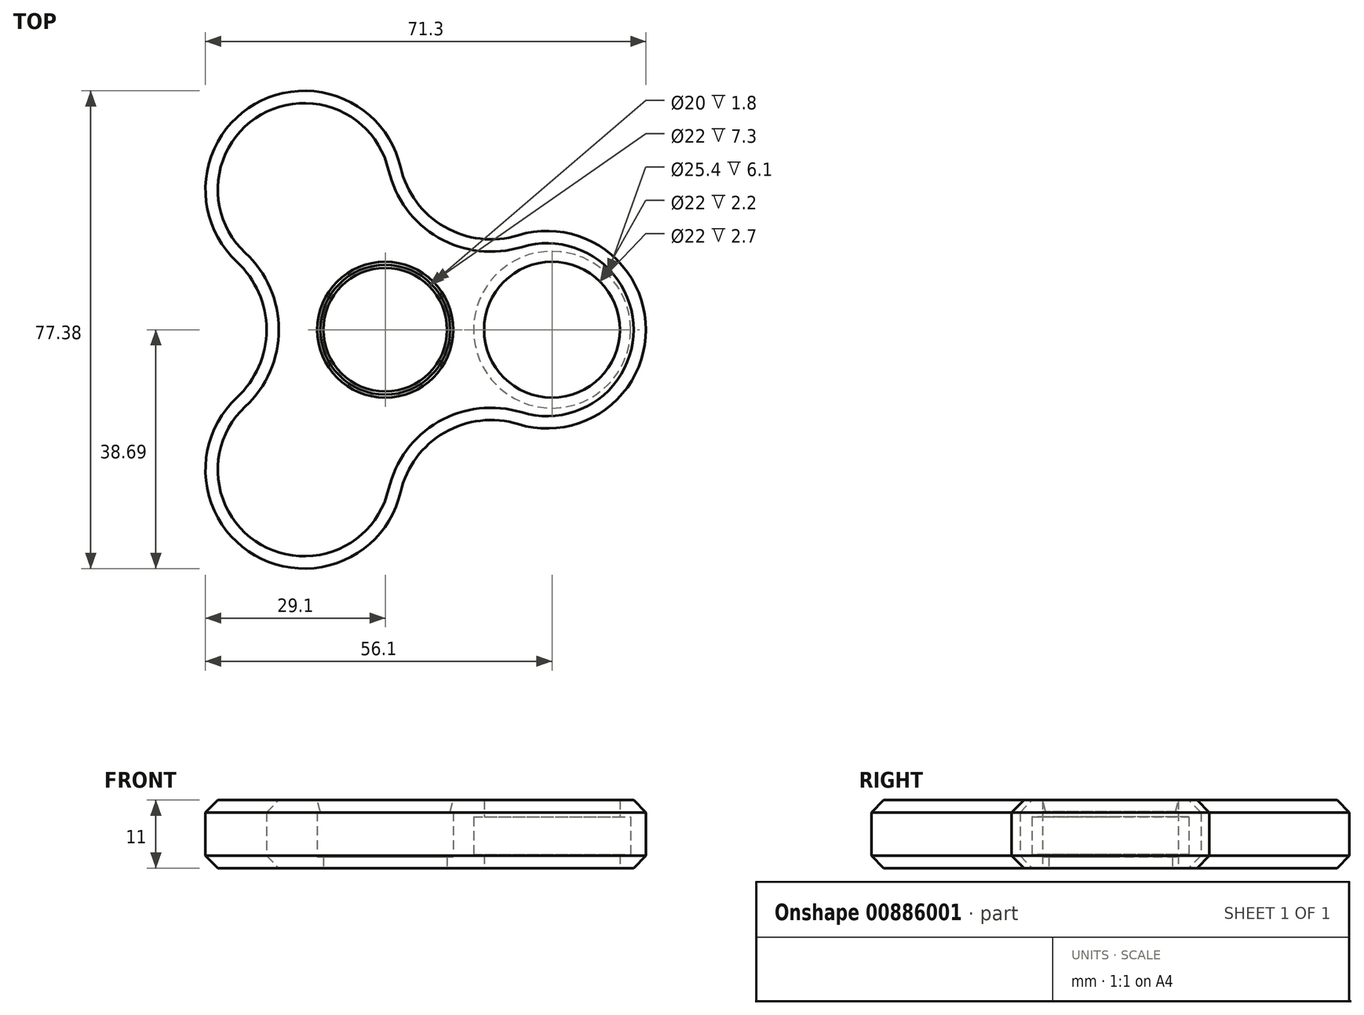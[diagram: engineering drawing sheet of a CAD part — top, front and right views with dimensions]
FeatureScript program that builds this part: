
annotation { "Feature Type Name" : "Feature", "Feature Type Description" : "" }
export const myFeature = defineFeature(function(context is Context, id is Id, definition is map)
    precondition{}
    {
        {
            var Q0;
            Q0=qCreatedBy(makeId("Top.planeOp"),FACE);
            var sketch = newSketch(context, id + "F0", { "sketchPlane" : qUnion([Q0])});
            skLineSegment(sketch, "E0", {"start": v(0, 0) * mm, "end": v(26.2, 0) * mm, "construction": true});
            skCircle(sketch, "E1", {"center": v(0, 0) * mm, "radius": 26.2 * mm, "construction": true});
            skLineSegment(sketch, "E2", {"start": v(0, 0) * mm, "end": v(-13.1, 22.69) * mm, "construction": true});
            skLineSegment(sketch, "E3", {"start": v(0, 0) * mm, "end": v(-13.1, -22.69) * mm, "construction": true});
            skArc(sketch, "E4", {"start": v(21.5, -15.3) * mm, "mid": v(42.2, 0) * mm, "end": v(21.5, 15.3) * mm});
            skArc(sketch, "E5", {"start": v(2.5, 26.28) * mm, "mid": v(-21.1, 36.55) * mm, "end": v(-24, 10.98) * mm});
            skArc(sketch, "E6", {"start": v(-24, -10.98) * mm, "mid": v(-21.1, -36.55) * mm, "end": v(2.5, -26.28) * mm});
            skArc(sketch, "E7", {"start": v(2.5, 26.28) * mm, "mid": v(9.61, 16.65) * mm, "end": v(21.5, 15.3) * mm});
            skArc(sketch, "E8.1.0", {"start": v(-24, -10.98) * mm, "mid": v(-19.22, 0) * mm, "end": v(-24, 10.98) * mm});
            skArc(sketch, "E8.2.0", {"start": v(21.5, -15.3) * mm, "mid": v(9.61, -16.65) * mm, "end": v(2.5, -26.28) * mm});
            skSolve(sketch);
        }
        {
            var Q0;
            Q0=qSketchRegion(id+"F0",true);
            extrude(context, id + "F1", {"entities" : qUnion([Q0]), "depth" : 11 * mm, "offsetDistance" : 25 * mm});
        }
        {
            var Q0;
            Q0=qCreatedBy(makeId("Right.planeOp"),FACE);
            var sketch = newSketch(context, id + "F2", { "sketchPlane" : qUnion([Q0])});
            skLineSegment(sketch, "E9", {"start": v(0, 0) * mm, "end": v(0, 11) * mm});
            skLineSegment(sketch, "E10", {"start": v(0, 11) * mm, "end": v(11, 11) * mm});
            skLineSegment(sketch, "E11", {"start": v(11, 11) * mm, "end": v(10.5, 9.1) * mm});
            skLineSegment(sketch, "E12", {"start": v(10.5, 9.1) * mm, "end": v(11, 9.1) * mm});
            skLineSegment(sketch, "E13", {"start": v(11, 9.1) * mm, "end": v(11, 1.8) * mm});
            skLineSegment(sketch, "E14", {"start": v(11, 1.8) * mm, "end": v(10, 1.8) * mm});
            skLineSegment(sketch, "E15", {"start": v(10, 1.8) * mm, "end": v(10, 0) * mm});
            skLineSegment(sketch, "E16", {"start": v(10, 0) * mm, "end": v(0, 0) * mm});
            skLineSegment(sketch, "E17", {"start": v(0, 17.58) * mm, "end": v(0, -10.03) * mm, "construction": true});
            skSolve(sketch);
        }
        {
            var Q0;
            Q0=qSketchRegion(id+"F2",true);
            var Q1;
            Q1=sQuery(id+"F2.wireOp",EDGE,"E17");
            revolve(context, id + "F3", {"operationType" : NewBodyOperationType.REMOVE, "surfaceOperationType" : NewSurfaceOperationType.NEW, "entities" : qUnion([Q0]), "axis" : qUnion([Q1]), "revolveType" : RevolveType.FULL, "oppositeDirection" : true});
        }
        {
            var Q0;
            Q0=qCreatedBy(makeId("Front.planeOp"),FACE);
            var sketch = newSketch(context, id + "F4", { "sketchPlane" : qUnion([Q0])});
            skLineSegment(sketch, "E18", {"start": v(27, 31.94) * mm, "end": v(27, -19.35) * mm, "construction": true});
            skLineSegment(sketch, "E19", {"start": v(27, 0) * mm, "end": v(27, 11) * mm});
            skLineSegment(sketch, "E20", {"start": v(27, 11) * mm, "end": v(14.3, 11) * mm});
            skLineSegment(sketch, "E21", {"start": v(16, 8.3) * mm, "end": v(14.3, 8.3) * mm});
            skLineSegment(sketch, "E22", {"start": v(14.3, 8.3) * mm, "end": v(14.3, 2.2) * mm});
            skLineSegment(sketch, "E23", {"start": v(14.3, 2.2) * mm, "end": v(16, 2.2) * mm});
            skLineSegment(sketch, "E24", {"start": v(16, 2.2) * mm, "end": v(16, 0) * mm});
            skLineSegment(sketch, "E25", {"start": v(16, 0) * mm, "end": v(27, 0) * mm});
            skLineSegment(sketch, "E26", {"start": v(16, 8.3) * mm, "end": v(16, 11) * mm});
            skSolve(sketch);
        }
        {
            var Q0;
            Q0=qSketchRegion(id+"F4",true);
            var Q1;
            Q1=sQuery(id+"F4.wireOp",EDGE,"E18");
            revolve(context, id + "F5", {"operationType" : NewBodyOperationType.REMOVE, "surfaceOperationType" : NewSurfaceOperationType.NEW, "entities" : qUnion([Q0]), "axis" : qUnion([Q1]), "revolveType" : RevolveType.FULL, "oppositeDirection" : true});
        }
        {
            var Q0;
            Q0=makeQuery(id+"F1.opExtrude","CAP_EDGE",EDGE,{"disambiguationData":[OSD([sQuery(id+"F0.wireOp",EDGE,"E8.2.0")])],"isStart":false});
            chamfer(context, id + "F6", {"entities" : qUnion([Q0]), "width" : 2 * mm, "tangentPropagation" : true});
        }
        {
            var Q0;
            Q0=makeQuery(id+"F1.opExtrude","CAP_EDGE",EDGE,{"disambiguationData":[OSD([sQuery(id+"F0.wireOp",EDGE,"E8.2.0")])],"isStart":true});
            chamfer(context, id + "F7", {"entities" : qUnion([Q0]), "width" : 2 * mm, "tangentPropagation" : true});
        }
    });
